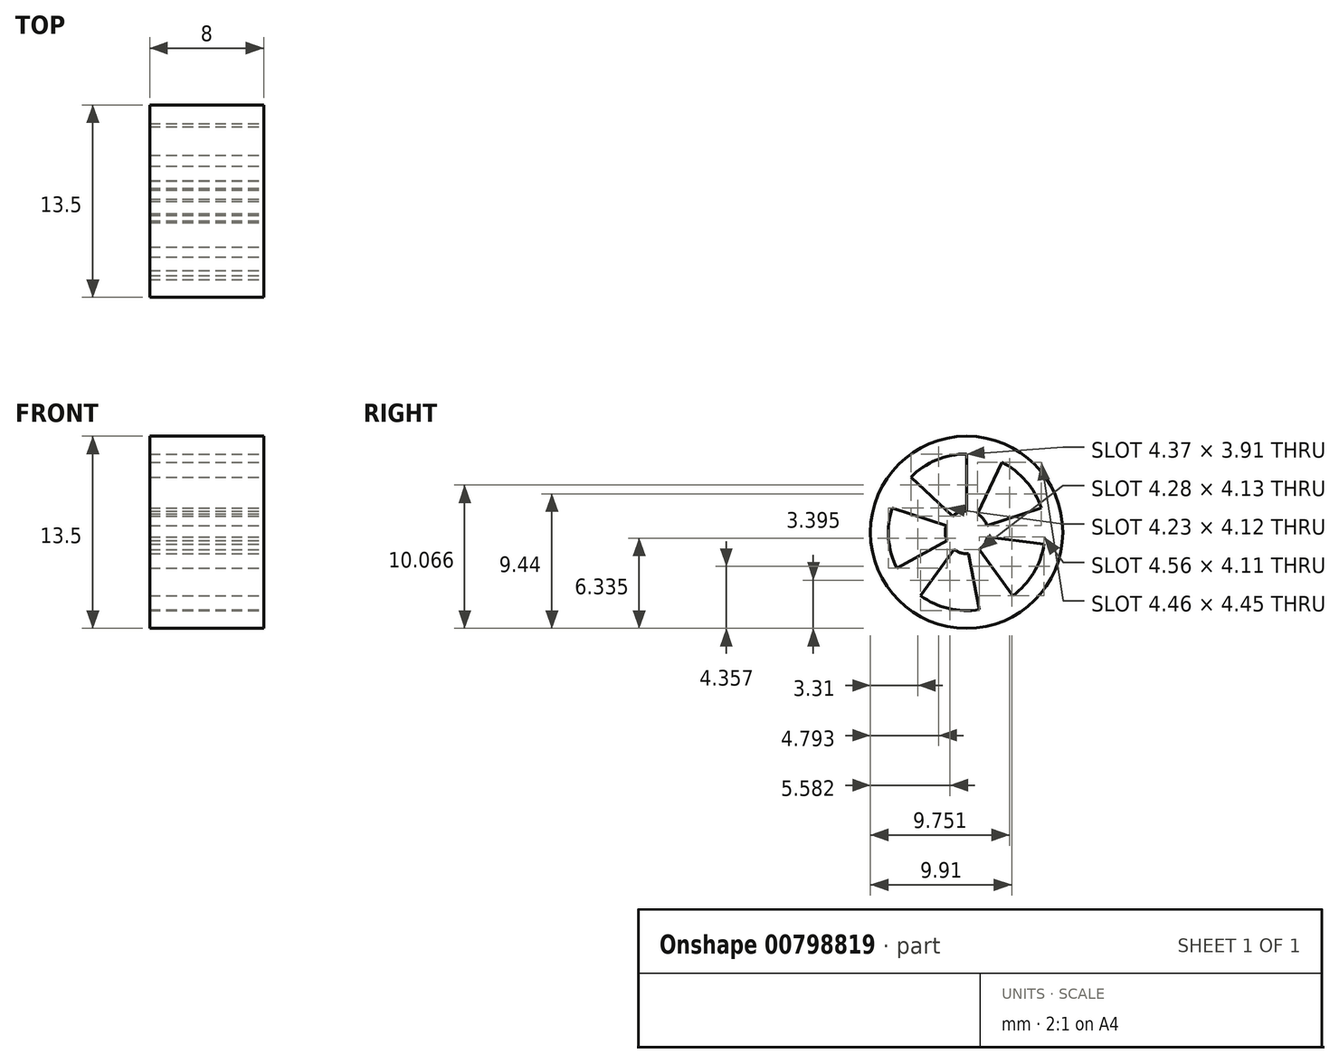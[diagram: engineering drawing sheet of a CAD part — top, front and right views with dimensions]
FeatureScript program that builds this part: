
annotation { "Feature Type Name" : "Feature", "Feature Type Description" : "" }
export const myFeature = defineFeature(function(context is Context, id is Id, definition is map)
    precondition{}
    {
        {
            var Q0;
            Q0=qCreatedBy(makeId("Right.planeOp"),FACE);
            var sketch = newSketch(context, id + "F0", { "sketchPlane" : qUnion([Q0])});
            skCircle(sketch, "E0", {"center": v(0, 0) * mm, "radius": 6.75 * mm});
            skSolve(sketch);
        }
        {
            var Q0;
            Q0 = qSketchRegion(id + "F0", true);
            extrude(context, id + "F1", {"entities" : qUnion([Q0]), "depth" : 8 * mm, "offsetDistance" : 25.4 * mm});
        }
        {
            var Q0;
            Q0=makeQuery(id+"F1.opExtrude","CAP_FACE",FACE,{"disambiguationData":[OSD([sQuery(id+"F0.wireOp",EDGE,"E0")])],"isStart":false});
            var sketch = newSketch(context, id + "F2", { "sketchPlane" : qUnion([Q0])});
            skCircle(sketch, "E1", {"center": v(0, 0) * mm, "radius": 5.5 * mm});
            skArc(sketch, "E2", {"start": v(0, 1.5) * mm, "mid": v(-0.4, -1.45) * mm, "end": v(0.77, 1.29) * mm});
            skLineSegment(sketch, "E3", {"start": v(0, 1.5) * mm, "end": v(0, 5.5) * mm});
            skLineSegment(sketch, "E4", {"start": v(0.77, 1.29) * mm, "end": v(2.46, 4.92) * mm});
            skLineSegment(sketch, "E5.1.0", {"start": v(-1.43, 0.46) * mm, "end": v(-5.23, 1.7) * mm});
            skLineSegment(sketch, "E5.1.1", {"start": v(-0.98, 1.13) * mm, "end": v(-3.91, 3.86) * mm});
            skLineSegment(sketch, "E5.2.0", {"start": v(-0.88, -1.21) * mm, "end": v(-3.23, -4.45) * mm});
            skLineSegment(sketch, "E5.2.1", {"start": v(-1.38, -0.59) * mm, "end": v(-4.88, -2.53) * mm});
            skLineSegment(sketch, "E5.3.0", {"start": v(0.88, -1.21) * mm, "end": v(3.23, -4.45) * mm});
            skLineSegment(sketch, "E5.3.1", {"start": v(0.13, -1.5) * mm, "end": v(0.9, -5.43) * mm});
            skLineSegment(sketch, "E5.4.0", {"start": v(1.43, 0.46) * mm, "end": v(5.23, 1.7) * mm});
            skLineSegment(sketch, "E5.4.1", {"start": v(1.46, -0.34) * mm, "end": v(5.44, -0.82) * mm});
            skSolve(sketch);
        }
        {
            var Q0;
            {var subQ0=sQuery(id+"F2.wireOp",EDGE,"E3");Q0=makeQuery(id+"F2.imprint","IMPRINT",FACE,{"disambiguationData":[TD([[makeQuery(id+"F2.imprint","IMPRINT",EDGE,{"derivedFrom":subQ0}),1.0]])]});}
            var Q1;
            {var subQ0=sQuery(id+"F2.wireOp",EDGE,"E4");Q1=makeQuery(id+"F2.imprint","IMPRINT",FACE,{"disambiguationData":[TD([[makeQuery(id+"F2.imprint","IMPRINT",EDGE,{"derivedFrom":subQ0}),-1.0]])]});}
            var Q2;
            {var subQ0=sQuery(id+"F2.wireOp",EDGE,"E5.3.0");Q2=makeQuery(id+"F2.imprint","IMPRINT",FACE,{"disambiguationData":[TD([[makeQuery(id+"F2.imprint","IMPRINT",EDGE,{"derivedFrom":subQ0}),1.0]])]});}
            var Q3;
            {var subQ0=sQuery(id+"F2.wireOp",EDGE,"E5.2.0");Q3=makeQuery(id+"F2.imprint","IMPRINT",FACE,{"disambiguationData":[TD([[makeQuery(id+"F2.imprint","IMPRINT",EDGE,{"derivedFrom":subQ0}),1.0]])]});}
            var Q4;
            {var subQ0=sQuery(id+"F2.wireOp",EDGE,"E5.1.0");Q4=makeQuery(id+"F2.imprint","IMPRINT",FACE,{"disambiguationData":[TD([[makeQuery(id+"F2.imprint","IMPRINT",EDGE,{"derivedFrom":subQ0}),1.0]])]});}
            extrude(context, id + "F3", {"entities" : qUnion([Q0, Q1, Q2, Q3, Q4]), "operationType" : NewBodyOperationType.REMOVE, "endBound" : BoundingType.THROUGH_ALL, "oppositeDirection" : true, "depth" : 25.4 * mm, "offsetDistance" : 25.4 * mm});
        }
    });
